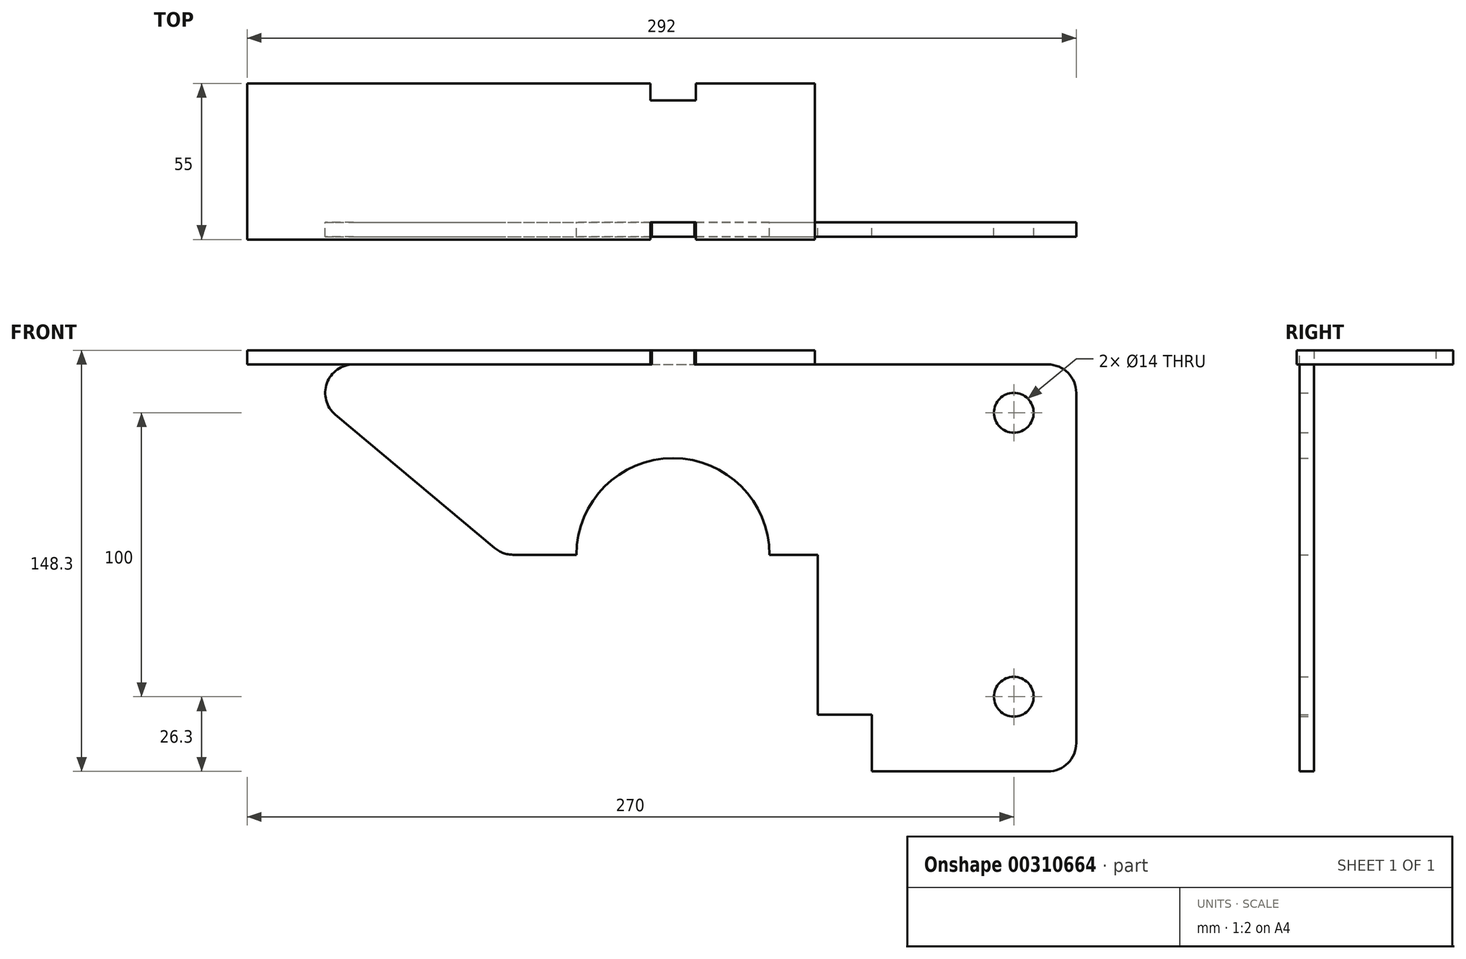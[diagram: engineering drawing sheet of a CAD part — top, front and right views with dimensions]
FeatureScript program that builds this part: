
annotation { "Feature Type Name" : "Feature", "Feature Type Description" : "" }
export const myFeature = defineFeature(function(context is Context, id is Id, definition is map)
    precondition{}
    {
        {
            var Q0;
            Q0=qCreatedBy(makeId("Front.planeOp"),FACE);
            var sketch = newSketch(context, id + "F0", { "sketchPlane" : qUnion([Q0])});
            skCircle(sketch, "E0", {"center": v(0, 0) * mm, "radius": 34 * mm, "construction": true});
            skLineSegment(sketch, "E1", {"start": v(-112.49, 67) * mm, "end": v(132, 67) * mm});
            skLineSegment(sketch, "E2", {"start": v(142, 57) * mm, "end": v(142, -66.3) * mm});
            skLineSegment(sketch, "E3", {"start": v(132, -76.3) * mm, "end": v(70, -76.3) * mm});
            skLineSegment(sketch, "E4", {"start": v(34, 0) * mm, "end": v(34, 0) * mm});
            skLineSegment(sketch, "E5", {"start": v(-56.37, 0) * mm, "end": v(-34, 0) * mm});
            skCircle(sketch, "E6", {"center": v(120, 50) * mm, "radius": 7 * mm});
            skCircle(sketch, "E7", {"center": v(120, -50) * mm, "radius": 7 * mm});
            skArc(sketch, "E8", {"start": v(34, 0) * mm, "mid": v(0, 34) * mm, "end": v(-34, 0) * mm});
            skLineSegment(sketch, "E9", {"start": v(34, 0) * mm, "end": v(51, 0) * mm});
            skPoint(sketch, "E10", {"position": v(51, 0) * mm});
            skLineSegment(sketch, "E11", {"start": v(51, 0) * mm, "end": v(51, -56.3) * mm});
            skLineSegment(sketch, "E12", {"start": v(51, -56.3) * mm, "end": v(70, -56.3) * mm});
            skLineSegment(sketch, "E13", {"start": v(70, -56.3) * mm, "end": v(70, -76.3) * mm});
            skLineSegment(sketch, "E14.bottom", {"start": v(-7.5, 67) * mm, "end": v(7.5, 67) * mm});
            skLineSegment(sketch, "E14.top", {"start": v(-7.5, 72) * mm, "end": v(7.5, 72) * mm});
            skLineSegment(sketch, "E14.left", {"start": v(-7.5, 67) * mm, "end": v(-7.5, 72) * mm});
            skLineSegment(sketch, "E14.right", {"start": v(7.5, 67) * mm, "end": v(7.5, 72) * mm});
            skPoint(sketch, "E15", {"position": v(0, 72) * mm});
            skPoint(sketch, "E16.visualSharp", {"position": v(142, 67) * mm});
            skArc(sketch, "E16.filletArc", {"start": v(142, 57) * mm, "mid": v(139.07, 64.07) * mm, "end": v(132, 67) * mm});
            skPoint(sketch, "E17.visualSharp", {"position": v(142, -76.3) * mm});
            skArc(sketch, "E17.filletArc", {"start": v(132, -76.3) * mm, "mid": v(139.07, -73.37) * mm, "end": v(142, -66.3) * mm});
            skLineSegment(sketch, "E18", {"start": v(-118.9, 49.33) * mm, "end": v(-62.79, 2.33) * mm});
            skPoint(sketch, "E19.visualSharp", {"position": v(-140, 67) * mm});
            skArc(sketch, "E19.filletArc", {"start": v(-112.49, 67) * mm, "mid": v(-121.88, 60.42) * mm, "end": v(-118.9, 49.33) * mm});
            skPoint(sketch, "E20.visualSharp", {"position": v(-60, 0) * mm});
            skArc(sketch, "E20.filletArc", {"start": v(-62.79, 2.33) * mm, "mid": v(-59.78, 0.6) * mm, "end": v(-56.37, 0) * mm});
            skSolve(sketch);
        }
        {
            var Q0;
            Q0 = qSketchRegion(id + "F0", true);
            extrude(context, id + "F1", {"entities" : qUnion([Q0]), "depth" : 5 * mm});
        }
        {
            var Q0;
            {var subQ0=sQuery(id+"F0.wireOp",EDGE,"E1");Q0=makeQuery(id+"F1.opExtrude","SWEPT_FACE",FACE,{"disambiguationData":[OSD([subQ0]),TDD([makeQuery(id+"F0.imprint","IMPRINT",EDGE,{"disambiguationData":[TD([[makeQuery(id+"F0.imprint","INTERSECT",VERTEX,{"derivedFrom":[sQuery(id+"F0.wireOp",EDGE,"Qq6vzx61-vcA7-Or1N-aunF-YzaSUn9qJwvq"),subQ0]}),-1.0]])],"derivedFrom":subQ0})])]});}
            var sketch = newSketch(context, id + "F2", { "sketchPlane" : qUnion([Q0])});
            skLineSegment(sketch, "E21.bottom", {"start": v(50, -6) * mm, "end": v(8, -6) * mm});
            skLineSegment(sketch, "E21.top", {"start": v(50, 49) * mm, "end": v(8, 49) * mm});
            skLineSegment(sketch, "E21.left", {"start": v(50, -6) * mm, "end": v(50, 49) * mm});
            skLineSegment(sketch, "E21.right", {"start": v(-150, -6) * mm, "end": v(-150, 49) * mm});
            skLineSegment(sketch, "E22.top", {"start": v(-8, 0) * mm, "end": v(8, 0) * mm});
            skLineSegment(sketch, "E22.left", {"start": v(-8, -6) * mm, "end": v(-8, 0) * mm});
            skLineSegment(sketch, "E22.right", {"start": v(8, -6) * mm, "end": v(8, 0) * mm});
            skLineSegment(sketch, "E23.trimOffspring", {"start": v(-8, -6) * mm, "end": v(-150, -6) * mm});
            skLineSegment(sketch, "E24.top", {"start": v(-8, 43) * mm, "end": v(8, 43) * mm});
            skLineSegment(sketch, "E24.left", {"start": v(-8, 49) * mm, "end": v(-8, 43) * mm});
            skLineSegment(sketch, "E24.right", {"start": v(8, 49) * mm, "end": v(8, 43) * mm});
            skLineSegment(sketch, "E25.trimOffspring", {"start": v(-8, 49) * mm, "end": v(-150, 49) * mm});
            skSolve(sketch);
        }
        {
            var Q0;
            Q0 = qSketchRegion(id + "F2", true);
            extrude(context, id + "F3", {"entities" : qUnion([Q0]), "depth" : 5 * mm});
        }
    });
